# Revit family: Desk_Accessory-Teknion-BASPE_Seat_Pad_Felt-R2018
name_source: partatom
category: Furniture
revit_build: Autodesk Revit 2018 (Build: 20190510_1515(x64)
units: mm (PartAtom-declared; Revit-internal decimal feet)

## family parameters
Always vertical = Yes
Cut with Voids When Loaded = No
OmniClass Number = 23.40.20.00
OmniClass Title = General Furniture and Specialties
Room Calculation Point = No
Shared = Yes
Work Plane-Based = Yes

## types (3) — shared parameters
Assembly Code = E2020200
Default Elevation = 48 "
Manufacturer = Teknion
Manufacturer Fax = 416.661.4586
Part Number = BASPE
Product Documentation Link = https://www.teknion.com
Product Line = Expansion Casegoods
Product Page URL = https://www.teknion.com
Series = Expansion Casegoods
Sustainability Data = https://www.teknion.com
URL = www.teknion.com
Unit Weight URL = http://www.teknion.com
Warranty = http://www.teknion.com

## per-type parameters (varying)
| type | Depth | Description | Model |
| 16" Depth | 16.185 " | Seat Pad - Felt, 16" Depth | BASPE16_ |
| 18" Depth | 18.185 " | Seat Pad - Felt, 18" Depth | BASPE18_ |
| 19" Depth | 19.039 " | Seat Pad - Felt, 19" Depth | BASPE19_ |

## geometry (parser evidence)
native form markers: Sweep x2
no freeform markers — native parametric forms only
